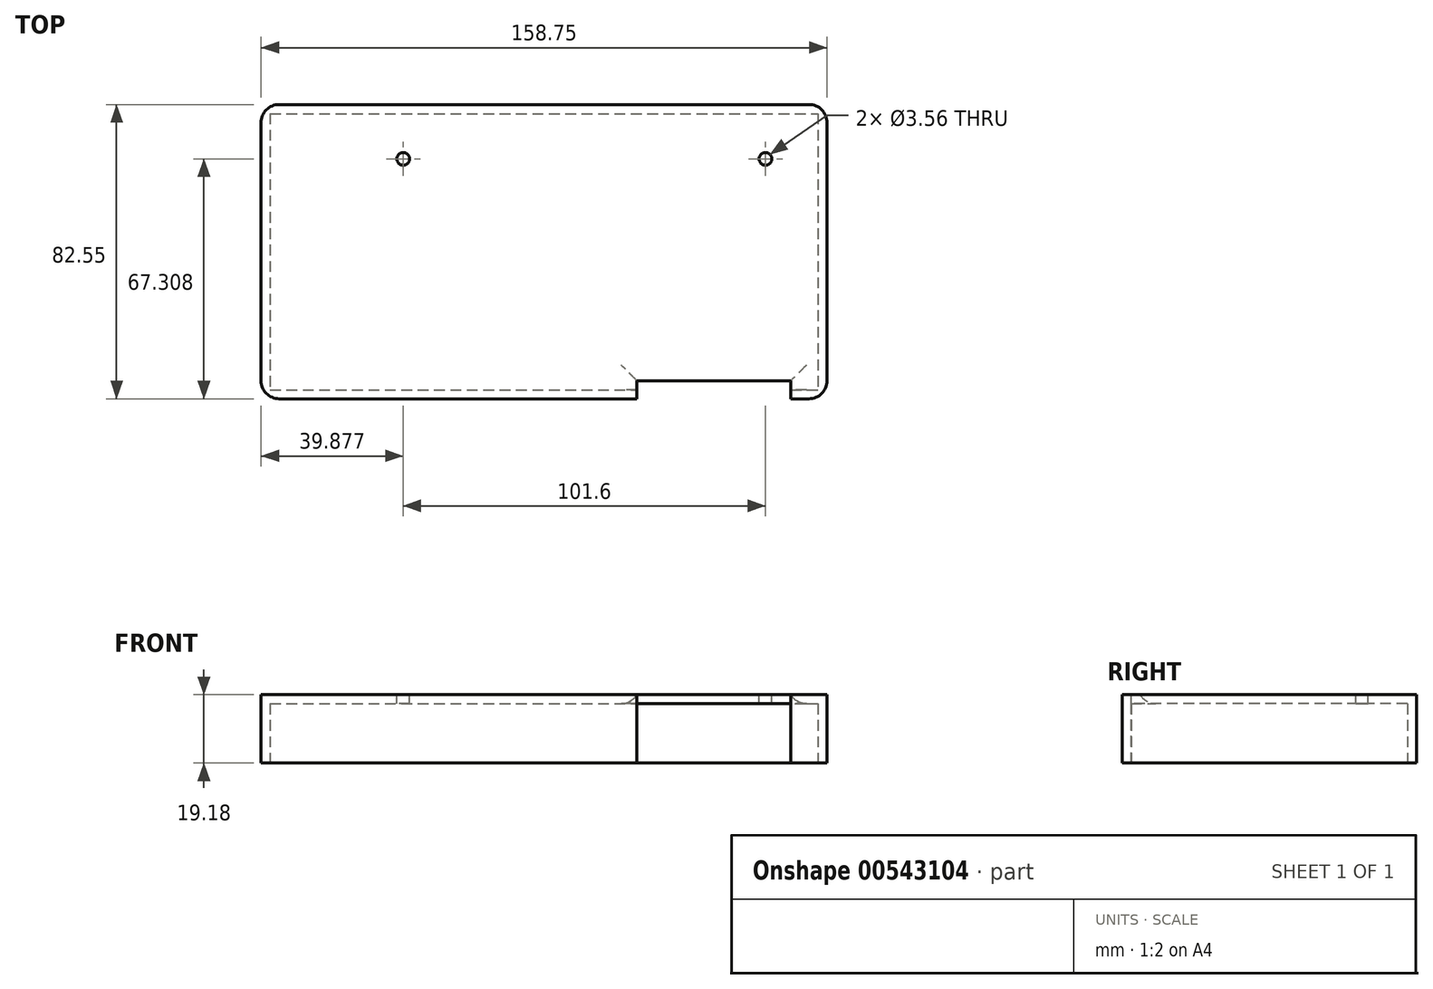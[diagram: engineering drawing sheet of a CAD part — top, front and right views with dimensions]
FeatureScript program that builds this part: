
annotation { "Feature Type Name" : "Feature", "Feature Type Description" : "" }
export const myFeature = defineFeature(function(context is Context, id is Id, definition is map)
    precondition{}
    {
        {
            var Q0;
            Q0=qCreatedBy(makeId("Top.planeOp"),FACE);
            var sketch = newSketch(context, id + "F0", { "sketchPlane" : qUnion([Q0])});
            skLineSegment(sketch, "E0.bottom", {"start": v(68.13, 45.3) * mm, "end": v(226.88, 45.3) * mm});
            skLineSegment(sketch, "E0.top", {"start": v(68.13, -37.25) * mm, "end": v(226.88, -37.25) * mm});
            skLineSegment(sketch, "E0.left", {"start": v(68.13, 45.3) * mm, "end": v(68.13, -37.25) * mm});
            skLineSegment(sketch, "E0.right", {"start": v(226.88, 45.3) * mm, "end": v(226.88, -37.25) * mm});
            skSolve(sketch);
        }
        {
            var Q0;
            Q0=makeQuery(id+"F0.imprint","IMPRINT",FACE,{"disambiguationData":[TD([[makeQuery(id+"F0.imprint","IMPRINT",EDGE,{"derivedFrom":sQuery(id+"F0.wireOp",EDGE,"E0.bottom")}),-1.0]])]});
            extrude(context, id + "F1", {"entities" : qUnion([Q0]), "depth" : 19.18 * mm, "offsetDistance" : 25.4 * mm});
        }
        {
            var Q0;
            Q0=makeQuery(id+"F1.opExtrude","CAP_FACE",FACE,{"disambiguationData":[OSD([sQuery(id+"F0.wireOp",EDGE,"E0.bottom"),sQuery(id+"F0.wireOp",EDGE,"E0.top"),sQuery(id+"F0.wireOp",EDGE,"E0.left"),sQuery(id+"F0.wireOp",EDGE,"E0.right")])],"isStart":true});
            shell(context, id + "F2", {"entities" : qUnion([Q0]), "thickness" : 2.54 * mm});
        }
        {
            var Q0;
            Q0=makeQuery(id+"F1.opExtrude","SWEPT_EDGE",EDGE,{"disambiguationData":[OSD([sQuery(id+"F0.wireOp",EDGE,"E0.top"),sQuery(id+"F0.wireOp",EDGE,"E0.right")])]});
            var Q1;
            Q1=makeQuery(id+"F1.opExtrude","SWEPT_EDGE",EDGE,{"disambiguationData":[OSD([sQuery(id+"F0.wireOp",EDGE,"E0.bottom"),sQuery(id+"F0.wireOp",EDGE,"E0.right")])]});
            var Q2;
            Q2=makeQuery(id+"F1.opExtrude","SWEPT_EDGE",EDGE,{"disambiguationData":[OSD([sQuery(id+"F0.wireOp",EDGE,"E0.bottom"),sQuery(id+"F0.wireOp",EDGE,"E0.left")])]});
            var Q3;
            Q3=makeQuery(id+"F1.opExtrude","SWEPT_EDGE",EDGE,{"disambiguationData":[OSD([sQuery(id+"F0.wireOp",EDGE,"E0.top"),sQuery(id+"F0.wireOp",EDGE,"E0.left")])]});
            fillet(context, id + "F3", {"entities" : qUnion([Q0, Q1, Q2, Q3]), "radius" : 5.08 * mm, "tangentPropagation" : true, "allowEdgeOverflow" : false});
        }
        {
            var Q0;
            Q0=makeQuery(id+"F1.opExtrude","CAP_FACE",FACE,{"disambiguationData":[OSD([sQuery(id+"F0.wireOp",EDGE,"E0.bottom"),sQuery(id+"F0.wireOp",EDGE,"E0.top"),sQuery(id+"F0.wireOp",EDGE,"E0.left"),sQuery(id+"F0.wireOp",EDGE,"E0.right")])],"isStart":false});
            var sketch = newSketch(context, id + "F4", { "sketchPlane" : qUnion([Q0])});
            skPoint(sketch, "E1", {"position": v(108, 30.06) * mm});
            skPoint(sketch, "E2", {"position": v(209.6, 30.06) * mm});
            skSolve(sketch);
        }
        {
            var Q0;
            Q0=sQuery(id+"F4.wireOp",VERTEX,"E1");
            var Q1;
            Q1=sQuery(id+"F4.wireOp",VERTEX,"E2");
            var Q2;
            Q2=makeQuery(id+"F1.opExtrude","SWEPT_BODY",BODY,{"disambiguationData":[OSD([sQuery(id+"F0.wireOp",EDGE,"E0.bottom"),sQuery(id+"F0.wireOp",EDGE,"E0.top"),sQuery(id+"F0.wireOp",EDGE,"E0.left"),sQuery(id+"F0.wireOp",EDGE,"E0.right")])]});
            hole(context, id + "F5", {"style" : HoleStyle.SIMPLE, "endStyle" : HoleEndStyle.THROUGH, "holeDiameter" : 3.56 * mm, "isTappedThrough" : true, "tappedDepth" : 12.7 * mm, "tapClearance" : 3, "locations" : qUnion([Q0, Q1]), "scope" : qUnion([Q2])});
        }
        {
            var Q0;
            Q0=makeQuery(id+"F1.opExtrude","SWEPT_FACE",FACE,{"disambiguationData":[OSD([sQuery(id+"F0.wireOp",EDGE,"E0.top")])]});
            var sketch = newSketch(context, id + "F6", { "sketchPlane" : qUnion([Q0])});
            skLineSegment(sketch, "E3", {"start": v(216.72, 19.18) * mm, "end": v(216.72, 0) * mm});
            skLineSegment(sketch, "E4", {"start": v(173.54, 19.18) * mm, "end": v(173.54, 0) * mm});
            skSolve(sketch);
        }
        {
            var Q0;
            {var subQ0=sQuery(id+"F6.wireOp",EDGE,"E3");Q0=makeQuery(id+"F6.imprint","IMPRINT",FACE,{"disambiguationData":[TD([[makeQuery(id+"F6.imprint","IMPRINT",EDGE,{"derivedFrom":subQ0}),-1.0]])]});}
            extrude(context, id + "F7", {"entities" : qUnion([Q0]), "operationType" : NewBodyOperationType.REMOVE, "oppositeDirection" : true, "depth" : 5.08 * mm, "offsetDistance" : 25.4 * mm});
        }
        {
            var Q0;
            {var subQ0=sQuery(id+"F0.wireOp",EDGE,"E0.top");Q0=makeQuery(id+"F7.boolean.opBoolean","INTERSECT",EDGE,{"derivedFrom":[makeQuery(id+"F2.opShell","OFFSET_FACE",FACE,{"disambiguationData":[OSD([sQuery(id+"F0.wireOp",EDGE,"E0.bottom"),subQ0,sQuery(id+"F0.wireOp",EDGE,"E0.left"),sQuery(id+"F0.wireOp",EDGE,"E0.right")])]}),makeQuery(id+"F7.opExtrude","CAP_FACE",FACE,{"disambiguationData":[OSD([subQ0,sQuery(id+"F6.wireOp",EDGE,"E3"),sQuery(id+"F6.wireOp",EDGE,"E4")])],"isStart":false})]});}
            var Q1;
            Q1=makeQuery(id+"F7.boolean.opBoolean","INTERSECT",EDGE,{"derivedFrom":[makeQuery(id+"F2.opShell","OFFSET_FACE",FACE,{"disambiguationData":[OSD([sQuery(id+"F0.wireOp",EDGE,"E0.bottom"),sQuery(id+"F0.wireOp",EDGE,"E0.top"),sQuery(id+"F0.wireOp",EDGE,"E0.left"),sQuery(id+"F0.wireOp",EDGE,"E0.right")])]}),makeQuery(id+"F7.opExtrude","SWEPT_FACE",FACE,{"disambiguationData":[OSD([sQuery(id+"F6.wireOp",EDGE,"E4")])]})]});
            var Q2;
            Q2=makeQuery(id+"F7.boolean.opBoolean","INTERSECT",EDGE,{"derivedFrom":[makeQuery(id+"F2.opShell","OFFSET_FACE",FACE,{"disambiguationData":[OSD([sQuery(id+"F0.wireOp",EDGE,"E0.bottom"),sQuery(id+"F0.wireOp",EDGE,"E0.top"),sQuery(id+"F0.wireOp",EDGE,"E0.left"),sQuery(id+"F0.wireOp",EDGE,"E0.right")])]}),makeQuery(id+"F7.opExtrude","SWEPT_FACE",FACE,{"disambiguationData":[OSD([sQuery(id+"F6.wireOp",EDGE,"E3")])]})]});
            fillet(context, id + "F8", {"entities" : qUnion([Q0, Q1, Q2]), "radius" : 5.08 * mm, "tangentPropagation" : true, "allowEdgeOverflow" : false});
        }
    });
